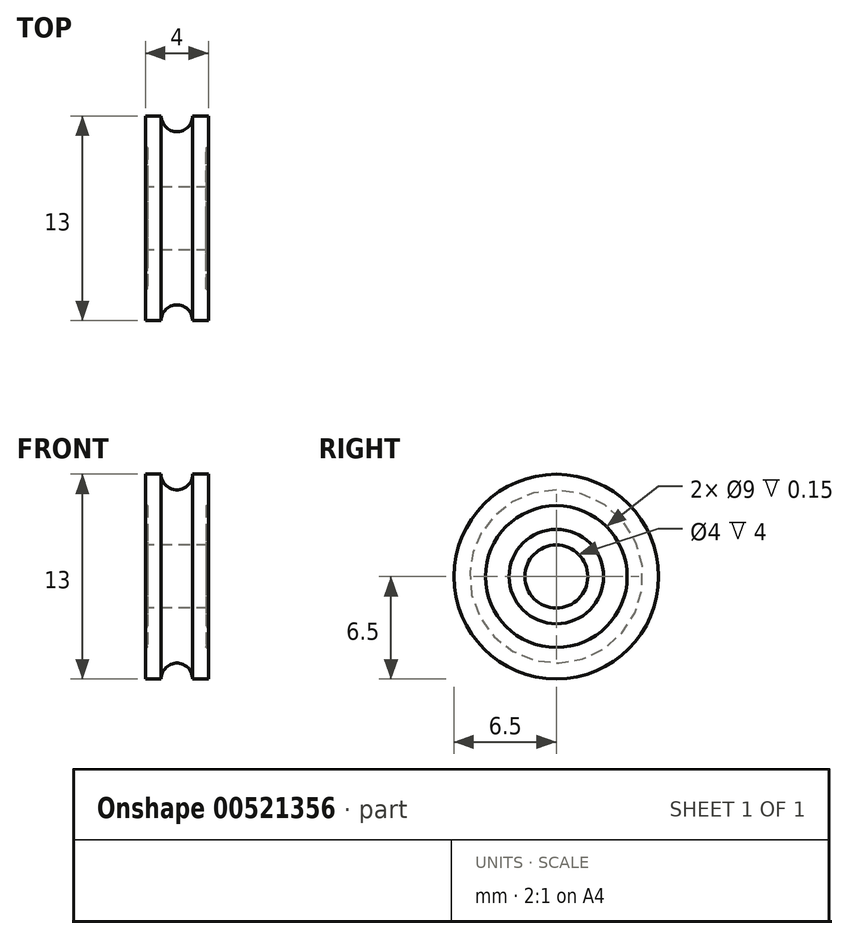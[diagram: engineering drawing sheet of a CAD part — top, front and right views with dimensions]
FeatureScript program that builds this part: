
annotation { "Feature Type Name" : "Feature", "Feature Type Description" : "" }
export const myFeature = defineFeature(function(context is Context, id is Id, definition is map)
    precondition{}
    {
        {
            var Q0;
            Q0=qCreatedBy(makeId("Front.planeOp"),FACE);
            var sketch = newSketch(context, id + "F0", { "sketchPlane" : qUnion([Q0])});
            skLineSegment(sketch, "E0", {"start": v(-17.08, 0) * mm, "end": v(16.32, 0) * mm, "construction": true});
            skLineSegment(sketch, "E1", {"start": v(0, 18.11) * mm, "end": v(0, -14.86) * mm, "construction": true});
            skLineSegment(sketch, "E2", {"start": v(0, 2) * mm, "end": v(-2, 2) * mm});
            skLineSegment(sketch, "E3", {"start": v(-2, 2) * mm, "end": v(-2, 3) * mm});
            skLineSegment(sketch, "E4", {"start": v(-2, 3) * mm, "end": v(-1.85, 3) * mm});
            skLineSegment(sketch, "E5", {"start": v(-1.85, 3) * mm, "end": v(-1.85, 4.5) * mm, "construction": true});
            skLineSegment(sketch, "E6", {"start": v(-1.85, 4.5) * mm, "end": v(-2, 4.5) * mm});
            skLineSegment(sketch, "E7", {"start": v(-2, 4.5) * mm, "end": v(-2, 6.5) * mm});
            skLineSegment(sketch, "E8", {"start": v(-2, 6.5) * mm, "end": v(-1, 6.5) * mm});
            skArc(sketch, "E9", {"start": v(-1, 6.5) * mm, "mid": v(-0.7, 5.8) * mm, "end": v(0, 5.5) * mm});
            skArc(sketch, "E10", {"start": v(-1.85, 4.5) * mm, "mid": v(-2, 3.75) * mm, "end": v(-1.85, 3) * mm});
            skLineSegment(sketch, "E11", {"start": v(0, 5.5) * mm, "end": v(0, 2) * mm});
            skSolve(sketch);
        }
        {
            var Q0;
            Q0 = qSketchRegion(id + "F0", true);
            var Q1;
            Q1=sQuery(id+"F0.wireOp",EDGE,"E0");
            revolve(context, id + "F1", {"entities" : qUnion([Q0]), "axis" : qUnion([Q1]), "revolveType" : RevolveType.FULL});
        }
        {
            var Q0;
            Q0=makeQuery(id+"F1.opRevolve","SWEPT_BODY",BODY,{"disambiguationData":[OSD([sQuery(id+"F0.wireOp",EDGE,"E2"),sQuery(id+"F0.wireOp",EDGE,"E3"),sQuery(id+"F0.wireOp",EDGE,"E4"),sQuery(id+"F0.wireOp",EDGE,"E6"),sQuery(id+"F0.wireOp",EDGE,"E7"),sQuery(id+"F0.wireOp",EDGE,"E8"),sQuery(id+"F0.wireOp",EDGE,"E9"),sQuery(id+"F0.wireOp",EDGE,"E10"),sQuery(id+"F0.wireOp",EDGE,"E11")])]});
            var Q1;
            Q1=makeQuery(id+"F1.opRevolve","SWEPT_FACE",FACE,{"disambiguationData":[OSD([sQuery(id+"F0.wireOp",EDGE,"E11")])]});
            mirror(context, id + "F2", {"operationType" : NewBodyOperationType.ADD, "entities" : qUnion([Q0]), "mirrorPlane" : qUnion([Q1])});
        }
    });
